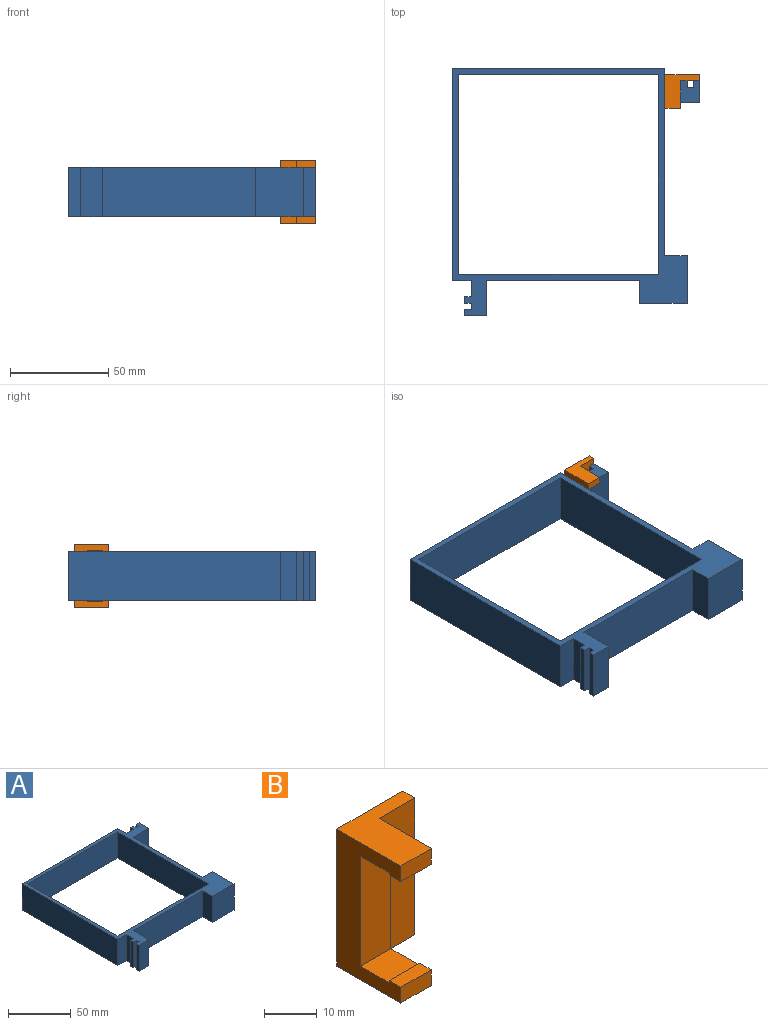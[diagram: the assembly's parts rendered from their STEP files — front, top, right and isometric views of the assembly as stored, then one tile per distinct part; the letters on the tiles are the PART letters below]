
ASSEMBLY  parts=2 mates=1
PART A: 34 faces, bbox 125.7x125.7x25.4 mm
  f0: plane 78.11x25.4mm, normal (1,0,0), area 1983.9mm2, adj f10,f11,f21,f31
  f1: plane 78.11x25.4mm, normal (0,-1,0), area 1983.9mm2, adj f10,f11,f17,f30
  f2: plane 25.4x9.53mm, normal (1,0,0), area 241.9mm2, adj f3,f10,f11,f29
  f3: plane 107.95x25.4mm, normal (0,1,0), area 2741.9mm2, adj f2,f4,f10,f11
  f4: plane 107.95x25.4mm, normal (-1,0,0), area 2741.9mm2, adj f3,f9,f10,f11
  f5: plane 101.6x25.4mm, normal (1,0,0), area 2580.6mm2, adj f6,f8,f10,f11
  f6: plane 101.6x25.4mm, normal (0,-1,0), area 2580.6mm2, adj f5,f7,f10,f11
  f7: plane 101.6x25.4mm, normal (-1,0,0), area 2580.6mm2, adj f6,f8,f10,f11
  f8: plane 101.6x25.4mm, normal (0,1,0), area 2580.6mm2, adj f5,f7,f10,f11
  f9: plane 25.4x9.53mm, normal (0,-1,0), area 241.9mm2, adj f4,f10,f11,f18
  f10: plane 125.73x125.73mm, normal (0,0,1), area 2062.9mm2, adj f0,f1,f2,f3,f4,f5,f6,f7
  f11: plane 125.73x125.73mm, normal (0,0,-1), area 2062.9mm2, adj f0,f1,f2,f3,f4,f5,f6,f7
  f12: plane 25.4x3.18mm, normal (0,-1,0), area 80.6mm2, adj f10,f11,f13,f20
  f13: plane 25.4x3.18mm, normal (-1,0,0), area 80.6mm2, adj f10,f11,f12,f14
  f14: plane 25.4x3.18mm, normal (0,1,0), area 80.6mm2, adj f10,f11,f13,f15
  f15: plane 25.4x3.18mm, normal (-1,0,0), area 80.6mm2, adj f10,f11,f14,f16
  f16: plane 25.4x10.8mm, normal (0,-1,0), area 274.2mm2, adj f10,f11,f15,f17
  f17: plane 25.4x17.78mm, normal (1,0,0), area 451.6mm2, adj f1,f10,f11,f16
  f18: plane 25.4x8.26mm, normal (-1,0,0), area 209.7mm2, adj f9,f10,f11,f19
  f19: plane 25.4x3.18mm, normal (0,1,0), area 80.6mm2, adj f10,f11,f18,f20
  f20: plane 25.4x3.18mm, normal (-1,0,0), area 80.6mm2, adj f10,f11,f12,f19
  f21: plane 25.4x17.78mm, normal (0,-1,0), area 451.6mm2, adj f0,f10,f11,f22
  f22: plane 25.4x10.8mm, normal (1,0,0), area 274.2mm2, adj f10,f11,f21,f23
  f23: plane 25.4x3.18mm, normal (0,1,0), area 80.6mm2, adj f10,f11,f22,f24
  f24: plane 25.4x3.18mm, normal (-1,0,0), area 80.6mm2, adj f10,f11,f23,f25
  f25: plane 25.4x3.18mm, normal (0,1,0), area 80.6mm2, adj f10,f11,f24,f26
  f26: plane 25.4x3.18mm, normal (1,0,0), area 80.6mm2, adj f10,f11,f25,f27
  f27: plane 25.4x3.18mm, normal (0,1,0), area 80.6mm2, adj f10,f11,f26,f28
  f28: plane 25.4x3.18mm, normal (-1,0,0), area 80.6mm2, adj f10,f11,f27,f29
  f29: plane 25.4x8.26mm, normal (0,1,0), area 209.7mm2, adj f2,f10,f11,f28
  f30: plane 25.4x11.43mm, normal (-1,0,0), area 290.3mm2, adj f1,f10,f11,f33
  f31: plane 25.4x11.43mm, normal (0,1,0), area 290.3mm2, adj f0,f10,f11,f32
  f32: plane 25.4x24.13mm, normal (1,0,0), area 612.9mm2, adj f10,f11,f31,f33
  f33: plane 25.4x24.13mm, normal (0,-1,0), area 612.9mm2, adj f10,f11,f30,f32
PART B: 16 faces, bbox 17.7x17.1x31.8 mm
  f0: plane 17.65x17.15mm, normal (0,0,1), area 169.6mm2, adj f2,f9,f11,f12,f13,f15
  f1: plane 17.65x17.15mm, normal (0,0,-1), area 169.6mm2, adj f9,f10,f11,f12,f13,f15
  f2: plane 8.13x3.63mm, normal (0,-1,0), area 29.5mm2, adj f0,f3,f12,f15
  f3: plane 8.13x3.12mm, normal (0,0,-1), area 25.4mm2, adj f2,f7,f12,f15
  f4: plane 8.13x7.67mm, normal (0,0,1), area 62.3mm2, adj f6,f8,f12,f15
  f5: plane 8.13x7.67mm, normal (0,0,-1), area 62.3mm2, adj f7,f8,f12,f15
  f6: plane 8.13x0.51mm, normal (0,1,0), area 4.1mm2, adj f4,f12,f14,f15
  f7: plane 8.13x0.51mm, normal (0,1,0), area 4.1mm2, adj f3,f5,f12,f15
  f8: plane 25.5x8.13mm, normal (0,-1,0), area 207.3mm2, adj f4,f5,f12,f15
  f9: plane 31.75x3.18mm, normal (1,0,0), area 100.8mm2, adj f0,f1,f11,f13
  f10: plane 8.13x3.63mm, normal (0,-1,0), area 29.5mm2, adj f1,f12,f14,f15
  f11: plane 31.75x9.53mm, normal (0,-1,0), area 302.4mm2, adj f0,f1,f9,f12
  f12: plane 31.75x13.97mm, normal (1,0,0), area 171.4mm2, adj f0,f1,f2,f3,f4,f5,f6,f7
  f13: plane 31.75x17.65mm, normal (0,1,0), area 560.5mm2, adj f0,f1,f9,f15
  f14: plane 8.13x3.12mm, normal (0,0,1), area 25.4mm2, adj f6,f10,f12,f15
  f15: plane 31.75x17.15mm, normal (-1,0,0), area 272.2mm2, adj f0,f1,f2,f3,f4,f5,f6,f7
PLACE A t=(-24.38,45.13,-35.18)mm
PLACE B t=(78.55,45.13,-38.35)mm
MATE fastened A.f29 <-> B.f8  axis (0,1,0) through (84.52,38.78,-22.48)mm
